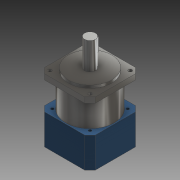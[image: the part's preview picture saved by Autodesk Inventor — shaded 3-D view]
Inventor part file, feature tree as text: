
AUTODESK INVENTOR PART (.ipt)
format: ipt  version: 2020 (Build 240168000, 168)  size: 220,672 bytes
history: native  units: mm
features: extrude x7, sketch x7, plane x1
ambient origin geometry x8: Origin, YZ Plane, XZ Plane, XY Plane, X Axis, Y Axis, Z Axis, Center Point
bodies: Solid1 (feature_tree)
feature tree (15):
  extrude  "Extrusion1"  Depth=94.0mm
  extrude  "Extrusion2"  Depth=105.0mm
  extrude  "Extrusion3"  Depth=37.125mm
  plane  "Work Plane1"
  extrude  "Extrusion4"  Depth=37.125mm
  extrude  "Extrusion5"  Depth=6.35mm
  extrude  "Extrusion6"  Depth=6.35mm
  extrude  "Extrusion7"  Depth=40.0mm
  sketch  "Sketch1"  dims[d0=94.0mm d1=47.0mm]
  sketch  "Sketch2"  dims[d2=47.0mm d3=105.0mm]
  sketch  "Sketch3"  dims[d4=74.25mm d5=37.125mm]
  sketch  "Sketch5"  dims[d6=74.25mm d7=37.125mm]
  sketch  "Sketch6"  dims[d8=6.35mm d9=6.35mm]
  sketch  "Sketch8"  dims[d10=6.35mm d11=6.35mm]
  sketch  "Sketch9"  dims[d12=9.8mm d13=9.8mm d14=9.8mm d15=9.8mm d16=9.8mm d17=9.8mm d18=9.8mm d19=9.8mm d20=10.0mm d21=0.0mm d22=80.0mm d23=5.0mm d24=0.0mm d25=20.0mm d26=50.0mm d27=0.0mm d28=-5.0mm d29=6.0mm d30=3.0mm d31=12.5mm d32=25.0mm d33=0.0mm d34=90.0mm d35=51.0mm d36=0.0mm d38=5.0mm d39=5.0mm d40=5.0mm d41=5.0mm d42=69.596mm d43=69.596mm d44=69.596mm d45=69.596mm d46=34.798mm d47=34.798mm d48=34.798mm d49=34.798mm d50=9.8mm d51=9.8mm d52=9.8mm d53=9.8mm d54=9.8mm d55=9.8mm d56=9.8mm d57=9.8mm d58=56.0mm d59=0.0mm d60=12.7mm d61=40.0mm d62=0.0mm]
